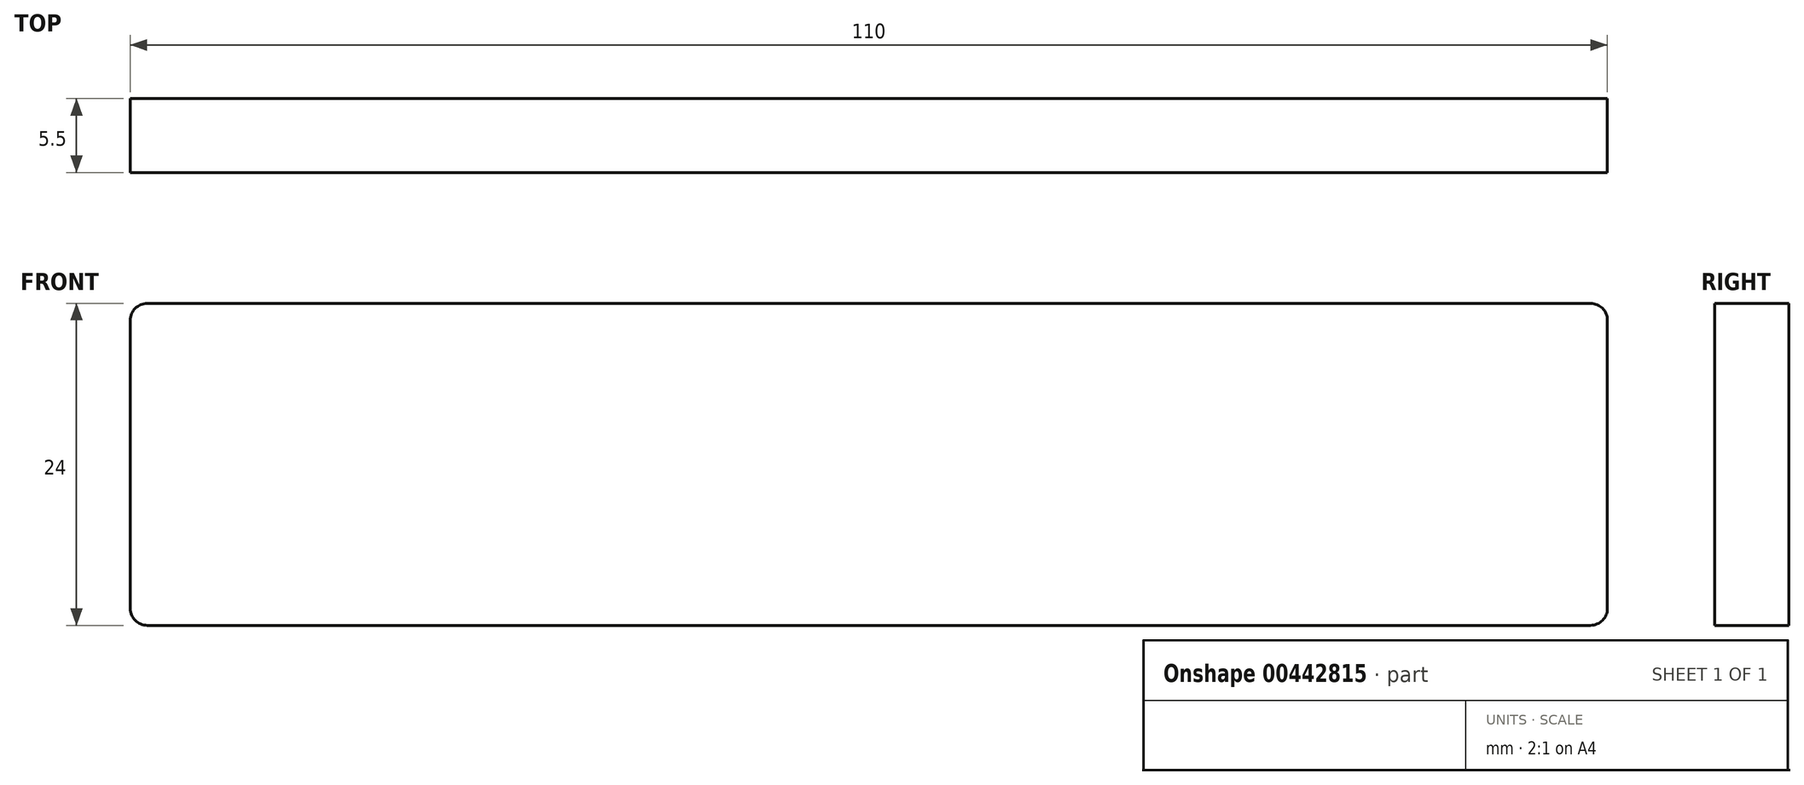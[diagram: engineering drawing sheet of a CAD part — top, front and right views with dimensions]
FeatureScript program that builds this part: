
annotation { "Feature Type Name" : "Feature", "Feature Type Description" : "" }
export const myFeature = defineFeature(function(context is Context, id is Id, definition is map)
    precondition{}
    {
        {
            var Q0;
            Q0=qCreatedBy(makeId("Front.planeOp"),FACE);
            var sketch = newSketch(context, id + "F0", { "sketchPlane" : qUnion([Q0])});
            skLineSegment(sketch, "E0.bottom", {"start": v(-1.27, 0) * mm, "end": v(-108.73, 0) * mm});
            skLineSegment(sketch, "E0.top", {"start": v(-1.27, 24) * mm, "end": v(-108.73, 24) * mm});
            skLineSegment(sketch, "E0.left", {"start": v(0, 1.27) * mm, "end": v(0, 22.73) * mm});
            skLineSegment(sketch, "E0.right", {"start": v(-110, 1.27) * mm, "end": v(-110, 22.73) * mm});
            skPoint(sketch, "E1.visualSharp", {"position": v(0, 24) * mm});
            skArc(sketch, "E1.filletArc", {"start": v(0, 22.73) * mm, "mid": v(-0.37, 23.63) * mm, "end": v(-1.27, 24) * mm});
            skPoint(sketch, "E2.visualSharp", {"position": v(-110, 24) * mm});
            skArc(sketch, "E2.filletArc", {"start": v(-108.73, 24) * mm, "mid": v(-109.63, 23.63) * mm, "end": v(-110, 22.73) * mm});
            skPoint(sketch, "E3.visualSharp", {"position": v(-110, 0) * mm});
            skArc(sketch, "E3.filletArc", {"start": v(-110, 1.27) * mm, "mid": v(-109.63, 0.37) * mm, "end": v(-108.73, 0) * mm});
            skPoint(sketch, "E4.visualSharp", {"position": v(0, 0) * mm});
            skArc(sketch, "E4.filletArc", {"start": v(-1.27, 0) * mm, "mid": v(-0.37, 0.37) * mm, "end": v(0, 1.27) * mm});
            skSolve(sketch);
        }
        {
            var Q0;
            Q0=qSketchRegion(id+"F0",true);
            extrude(context, id + "F1", {"entities" : qUnion([Q0]), "depth" : 5.5 * mm, "offsetDistance" : 25 * mm});
        }
    });
